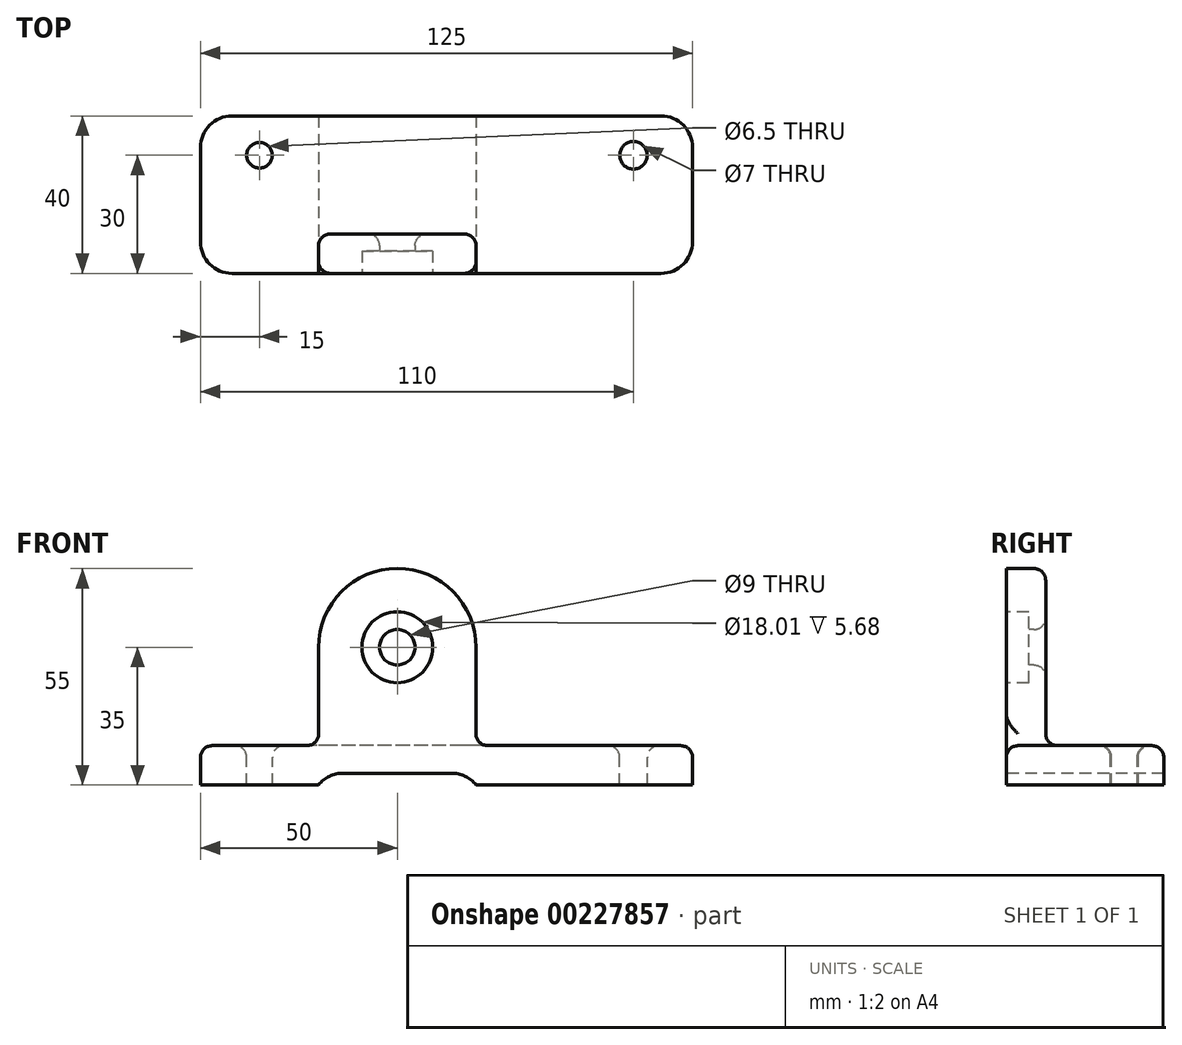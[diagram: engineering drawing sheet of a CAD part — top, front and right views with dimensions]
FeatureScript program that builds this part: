
annotation { "Feature Type Name" : "Feature", "Feature Type Description" : "" }
export const myFeature = defineFeature(function(context is Context, id is Id, definition is map)
    precondition{}
    {
        {
            var Q0;
            Q0=qCreatedBy(makeId("Top.planeOp"),FACE);
            var sketch = newSketch(context, id + "F0", { "sketchPlane" : qUnion([Q0])});
            skLineSegment(sketch, "E0.bottom", {"start": v(62.5, -20) * mm, "end": v(-62.5, -20) * mm});
            skLineSegment(sketch, "E0.top", {"start": v(62.5, 20) * mm, "end": v(-62.5, 20) * mm});
            skLineSegment(sketch, "E0.left", {"start": v(62.5, -20) * mm, "end": v(62.5, 20) * mm});
            skLineSegment(sketch, "E0.right", {"start": v(-62.5, -20) * mm, "end": v(-62.5, 20) * mm});
            skPoint(sketch, "E0.middle", {"position": v(0, 0) * mm});
            skSolve(sketch);
        }
        {
            var Q0;
            Q0=makeQuery(id+"F0.imprint","IMPRINT",FACE,{"disambiguationData":[TD([[makeQuery(id+"F0.imprint","IMPRINT",EDGE,{"derivedFrom":sQuery(id+"F0.wireOp",EDGE,"E0.bottom")}),-1.0]])]});
            extrude(context, id + "F1", {"entities" : qUnion([Q0]), "depth" : 10 * mm});
        }
        {
            var Q0;
            Q0=makeQuery(id+"F1.opExtrude","SWEPT_FACE",FACE,{"disambiguationData":[OSD([sQuery(id+"F0.wireOp",EDGE,"E0.bottom")])]});
            var sketch = newSketch(context, id + "F2", { "sketchPlane" : qUnion([Q0])});
            skLineSegment(sketch, "E1", {"start": v(-32.5, 10) * mm, "end": v(-32.5, 35) * mm});
            skLineSegment(sketch, "E2", {"start": v(7.5, 35) * mm, "end": v(7.5, 10) * mm});
            skArc(sketch, "E3", {"start": v(7.5, 35) * mm, "mid": v(-12.5, 55) * mm, "end": v(-32.5, 35) * mm});
            skSolve(sketch);
        }
        {
            var Q0;
            {var subQ0=sQuery(id+"F2.wireOp",EDGE,"E1");Q0=makeQuery(id+"F2.imprint","IMPRINT",FACE,{"disambiguationData":[TD([[makeQuery(id+"F2.imprint","IMPRINT",EDGE,{"derivedFrom":subQ0}),-1.0]])]});}
            extrude(context, id + "F3", {"entities" : qUnion([Q0]), "operationType" : NewBodyOperationType.ADD, "oppositeDirection" : true, "depth" : 10 * mm});
        }
        {
            var Q0;
            {var subQ0=sQuery(id+"F0.wireOp",EDGE,"E0.bottom");Q0=makeQuery(id+"F3.boolean.opBoolean","MERGE",FACE,{"derivedFrom":[makeQuery(id+"F1.opExtrude","SWEPT_FACE",FACE,{"disambiguationData":[OSD([subQ0])]}),makeQuery(id+"F3.opExtrude","CAP_FACE",FACE,{"disambiguationData":[OSD([subQ0,sQuery(id+"F2.wireOp",EDGE,"E1"),sQuery(id+"F2.wireOp",EDGE,"E2"),sQuery(id+"F2.wireOp",EDGE,"E3")])],"isStart":true})]});}
            var sketch = newSketch(context, id + "F4", { "sketchPlane" : qUnion([Q0])});
            skPoint(sketch, "E4", {"position": v(-12.5, 35) * mm});
            skSolve(sketch);
        }
        {
            var Q0;
            Q0=sQuery(id+"F4.wireOp",VERTEX,"E4");
            var Q1;
            Q1=makeQuery(id+"F1.opExtrude","SWEPT_BODY",BODY,{"disambiguationData":[OSD([sQuery(id+"F0.wireOp",EDGE,"E0.bottom"),sQuery(id+"F0.wireOp",EDGE,"E0.top"),sQuery(id+"F0.wireOp",EDGE,"E0.left"),sQuery(id+"F0.wireOp",EDGE,"E0.right")])]});
            hole(context, id + "F5", {"style" : HoleStyle.C_BORE, "endStyle" : HoleEndStyle.THROUGH, "holeDiameter" : 9 * mm, "cBoreDiameter" : 18.01 * mm, "cBoreDepth" : 5.68 * mm, "locations" : qUnion([Q0]), "scope" : qUnion([Q1]), "isTappedThrough" : true});
        }
        {
            var Q0;
            {var subQ0=sQuery(id+"F0.wireOp",EDGE,"E0.bottom");Q0=makeQuery(id+"F3.boolean.opBoolean","MERGE",FACE,{"derivedFrom":[makeQuery(id+"F1.opExtrude","SWEPT_FACE",FACE,{"disambiguationData":[OSD([subQ0])]}),makeQuery(id+"F3.opExtrude","CAP_FACE",FACE,{"disambiguationData":[OSD([subQ0,sQuery(id+"F2.wireOp",EDGE,"E1"),sQuery(id+"F2.wireOp",EDGE,"E2"),sQuery(id+"F2.wireOp",EDGE,"E3")])],"isStart":true})]});}
            var sketch = newSketch(context, id + "F6", { "sketchPlane" : qUnion([Q0])});
            skLineSegment(sketch, "E5", {"start": v(-32.5, 3) * mm, "end": v(7.5, 3) * mm});
            skLineSegment(sketch, "E6", {"start": v(-32.5, 3) * mm, "end": v(-32.5, 0) * mm});
            skLineSegment(sketch, "E7", {"start": v(7.5, 3) * mm, "end": v(7.5, 0) * mm});
            skLineSegment(sketch, "E8", {"start": v(-32.5, 0) * mm, "end": v(7.5, 0) * mm});
            skSolve(sketch);
        }
        {
            var Q0;
            Q0=makeQuery(id+"F6.imprint","IMPRINT",FACE,{"disambiguationData":[TD([[makeQuery(id+"F6.imprint","IMPRINT",EDGE,{"derivedFrom":sQuery(id+"F6.wireOp",EDGE,"E5")}),-1.0]])]});
            extrude(context, id + "F7", {"entities" : qUnion([Q0]), "operationType" : NewBodyOperationType.REMOVE, "endBound" : BoundingType.THROUGH_ALL, "oppositeDirection" : true, "depth" : 25 * mm});
        }
        {
            var Q0;
            Q0=makeQuery(id+"F7.boolean.opBoolean","COPY",EDGE,{"derivedFrom":makeQuery(id+"F7.opExtrude","SWEPT_EDGE",EDGE,{"disambiguationData":[OSD([sQuery(id+"F6.wireOp",EDGE,"E5"),sQuery(id+"F6.wireOp",EDGE,"E6")])]})});
            var Q1;
            Q1=makeQuery(id+"F7.boolean.opBoolean","COPY",EDGE,{"derivedFrom":makeQuery(id+"F7.opExtrude","SWEPT_EDGE",EDGE,{"disambiguationData":[OSD([sQuery(id+"F6.wireOp",EDGE,"E5"),sQuery(id+"F6.wireOp",EDGE,"E7")])]})});
            fillet(context, id + "F8", {"entities" : qUnion([Q0, Q1]), "radius" : 8 * mm, "tangentPropagation" : true, "allowEdgeOverflow" : false});
        }
        {
            var Q0;
            Q0=makeQuery(id+"F1.opExtrude","CAP_FACE",FACE,{"disambiguationData":[OSD([sQuery(id+"F0.wireOp",EDGE,"E0.bottom"),sQuery(id+"F0.wireOp",EDGE,"E0.top"),sQuery(id+"F0.wireOp",EDGE,"E0.left"),sQuery(id+"F0.wireOp",EDGE,"E0.right")])],"isStart":false});
            var sketch = newSketch(context, id + "F9", { "sketchPlane" : qUnion([Q0])});
            skCircle(sketch, "E9", {"center": v(-47.5, 10) * mm, "radius": 3.25 * mm});
            skSolve(sketch);
        }
        {
            var Q0;
            Q0=makeQuery(id+"F9.imprint","IMPRINT",FACE,{"disambiguationData":[TD([[makeQuery(id+"F9.imprint","IMPRINT",EDGE,{"derivedFrom":sQuery(id+"F9.wireOp",EDGE,"E9")}),1.0]])]});
            extrude(context, id + "F10", {"entities" : qUnion([Q0]), "operationType" : NewBodyOperationType.REMOVE, "endBound" : BoundingType.THROUGH_ALL, "oppositeDirection" : true, "depth" : 25 * mm});
        }
        {
            var Q0;
            Q0=makeQuery(id+"F1.opExtrude","CAP_FACE",FACE,{"disambiguationData":[OSD([sQuery(id+"F0.wireOp",EDGE,"E0.bottom"),sQuery(id+"F0.wireOp",EDGE,"E0.top"),sQuery(id+"F0.wireOp",EDGE,"E0.left"),sQuery(id+"F0.wireOp",EDGE,"E0.right")])],"isStart":false});
            var sketch = newSketch(context, id + "F11", { "sketchPlane" : qUnion([Q0])});
            skCircle(sketch, "E10", {"center": v(47.5, 10) * mm, "radius": 3.5 * mm});
            skSolve(sketch);
        }
        {
            var Q0;
            Q0=makeQuery(id+"F11.imprint","IMPRINT",FACE,{"disambiguationData":[TD([[makeQuery(id+"F11.imprint","IMPRINT",EDGE,{"derivedFrom":sQuery(id+"F11.wireOp",EDGE,"E10")}),1.0]])]});
            extrude(context, id + "F12", {"entities" : qUnion([Q0]), "operationType" : NewBodyOperationType.REMOVE, "oppositeDirection" : true, "depth" : 25 * mm});
        }
        {
            var Q0;
            Q0=makeQuery(id+"F1.opExtrude","SWEPT_EDGE",EDGE,{"disambiguationData":[OSD([sQuery(id+"F0.wireOp",EDGE,"E0.bottom"),sQuery(id+"F0.wireOp",EDGE,"E0.left")])]});
            var Q1;
            Q1=makeQuery(id+"F1.opExtrude","SWEPT_EDGE",EDGE,{"disambiguationData":[OSD([sQuery(id+"F0.wireOp",EDGE,"E0.bottom"),sQuery(id+"F0.wireOp",EDGE,"E0.right")])]});
            var Q2;
            Q2=makeQuery(id+"F1.opExtrude","SWEPT_EDGE",EDGE,{"disambiguationData":[OSD([sQuery(id+"F0.wireOp",EDGE,"E0.top"),sQuery(id+"F0.wireOp",EDGE,"E0.right")])]});
            var Q3;
            Q3=makeQuery(id+"F1.opExtrude","SWEPT_EDGE",EDGE,{"disambiguationData":[OSD([sQuery(id+"F0.wireOp",EDGE,"E0.top"),sQuery(id+"F0.wireOp",EDGE,"E0.left")])]});
            fillet(context, id + "F13", {"entities" : qUnion([Q0, Q1, Q2, Q3]), "radius" : 8 * mm, "tangentPropagation" : true, "allowEdgeOverflow" : false});
        }
        {
            var Q0;
            Q0=makeQuery(id+"F3.opExtrude","SWEPT_EDGE",EDGE,{"disambiguationData":[OSD([sQuery(id+"F0.wireOp",EDGE,"E0.bottom"),sQuery(id+"F2.wireOp",EDGE,"E2")])]});
            var Q1;
            Q1=makeQuery(id+"F3.opExtrude","SWEPT_EDGE",EDGE,{"disambiguationData":[OSD([sQuery(id+"F0.wireOp",EDGE,"E0.bottom"),sQuery(id+"F2.wireOp",EDGE,"E1")])]});
            var Q2;
            Q2=makeQuery(id+"F1.opExtrude","CAP_FACE",FACE,{"disambiguationData":[OSD([sQuery(id+"F0.wireOp",EDGE,"E0.bottom"),sQuery(id+"F0.wireOp",EDGE,"E0.top"),sQuery(id+"F0.wireOp",EDGE,"E0.left"),sQuery(id+"F0.wireOp",EDGE,"E0.right")])],"isStart":false});
            var Q3;
            Q3=makeQuery(id+"F3.opExtrude","CAP_FACE",FACE,{"disambiguationData":[OSD([sQuery(id+"F0.wireOp",EDGE,"E0.bottom"),sQuery(id+"F2.wireOp",EDGE,"E1"),sQuery(id+"F2.wireOp",EDGE,"E2"),sQuery(id+"F2.wireOp",EDGE,"E3")])],"isStart":false});
            fillet(context, id + "F14", {"entities" : qUnion([Q0, Q1, Q2, Q3]), "radius" : 3 * mm, "tangentPropagation" : true, "allowEdgeOverflow" : false});
        }
    });
